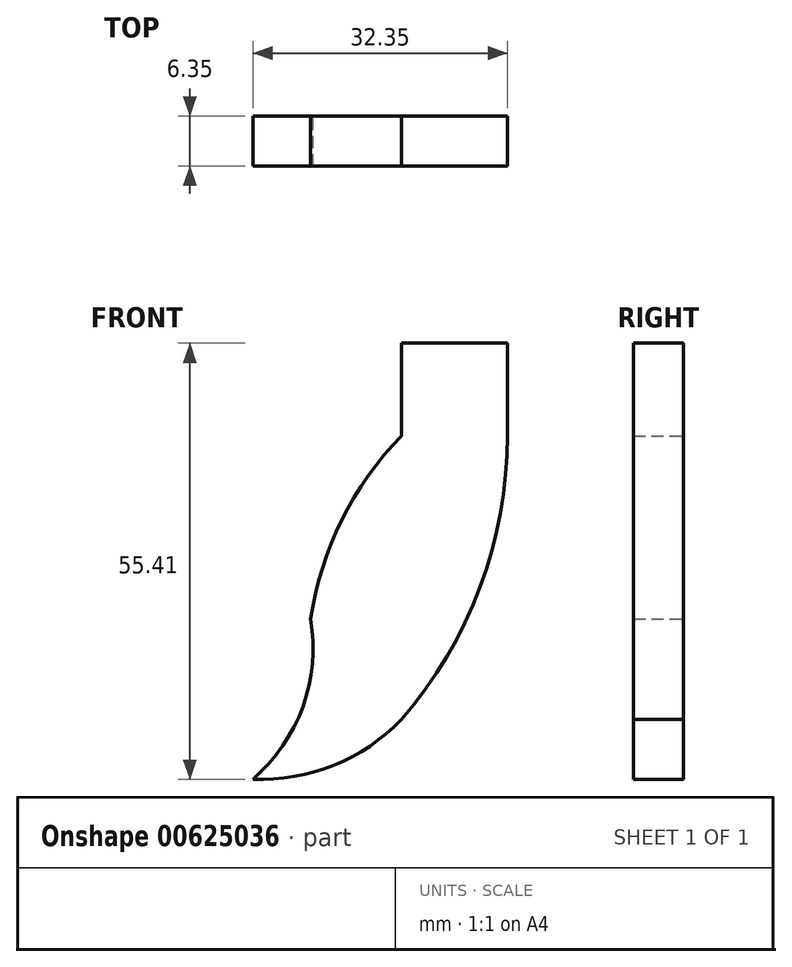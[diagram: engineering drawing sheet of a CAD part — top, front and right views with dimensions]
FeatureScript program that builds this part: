
annotation { "Feature Type Name" : "Feature", "Feature Type Description" : "" }
export const myFeature = defineFeature(function(context is Context, id is Id, definition is map)
    precondition{}
    {
        {
            var Q0;
            Q0=qCreatedBy(makeId("Front.planeOp"),FACE);
            var sketch = newSketch(context, id + "F0", { "sketchPlane" : qUnion([Q0])});
            skLineSegment(sketch, "E0", {"start": v(-18.26, 27.7) * mm, "end": v(-4.78, 27.7) * mm});
            skLineSegment(sketch, "E1", {"start": v(-4.78, 27.7) * mm, "end": v(-4.78, 15.93) * mm});
            skLineSegment(sketch, "E2", {"start": v(-18.26, 27.7) * mm, "end": v(-18.26, 15.93) * mm});
            skArc(sketch, "E3", {"start": v(-18.26, -20.1) * mm, "mid": v(-8.26, -3.3) * mm, "end": v(-4.78, 15.93) * mm});
            skArc(sketch, "E4", {"start": v(-37.13, -27.7) * mm, "mid": v(-26.86, -25.95) * mm, "end": v(-18.26, -20.1) * mm});
            skArc(sketch, "E5", {"start": v(-18.26, 15.93) * mm, "mid": v(-25.85, 5.2) * mm, "end": v(-29.77, -7.35) * mm});
            skArc(sketch, "E6", {"start": v(-37.13, -27.7) * mm, "mid": v(-30.77, -18.5) * mm, "end": v(-29.77, -7.35) * mm});
            skSolve(sketch);
        }
        {
            var Q0;
            Q0 = qSketchRegion(id + "F0", true);
            extrude(context, id + "F1", {"entities" : qUnion([Q0]), "depth" : 6.35 * mm, "offsetDistance" : 25.4 * mm});
        }
    });
